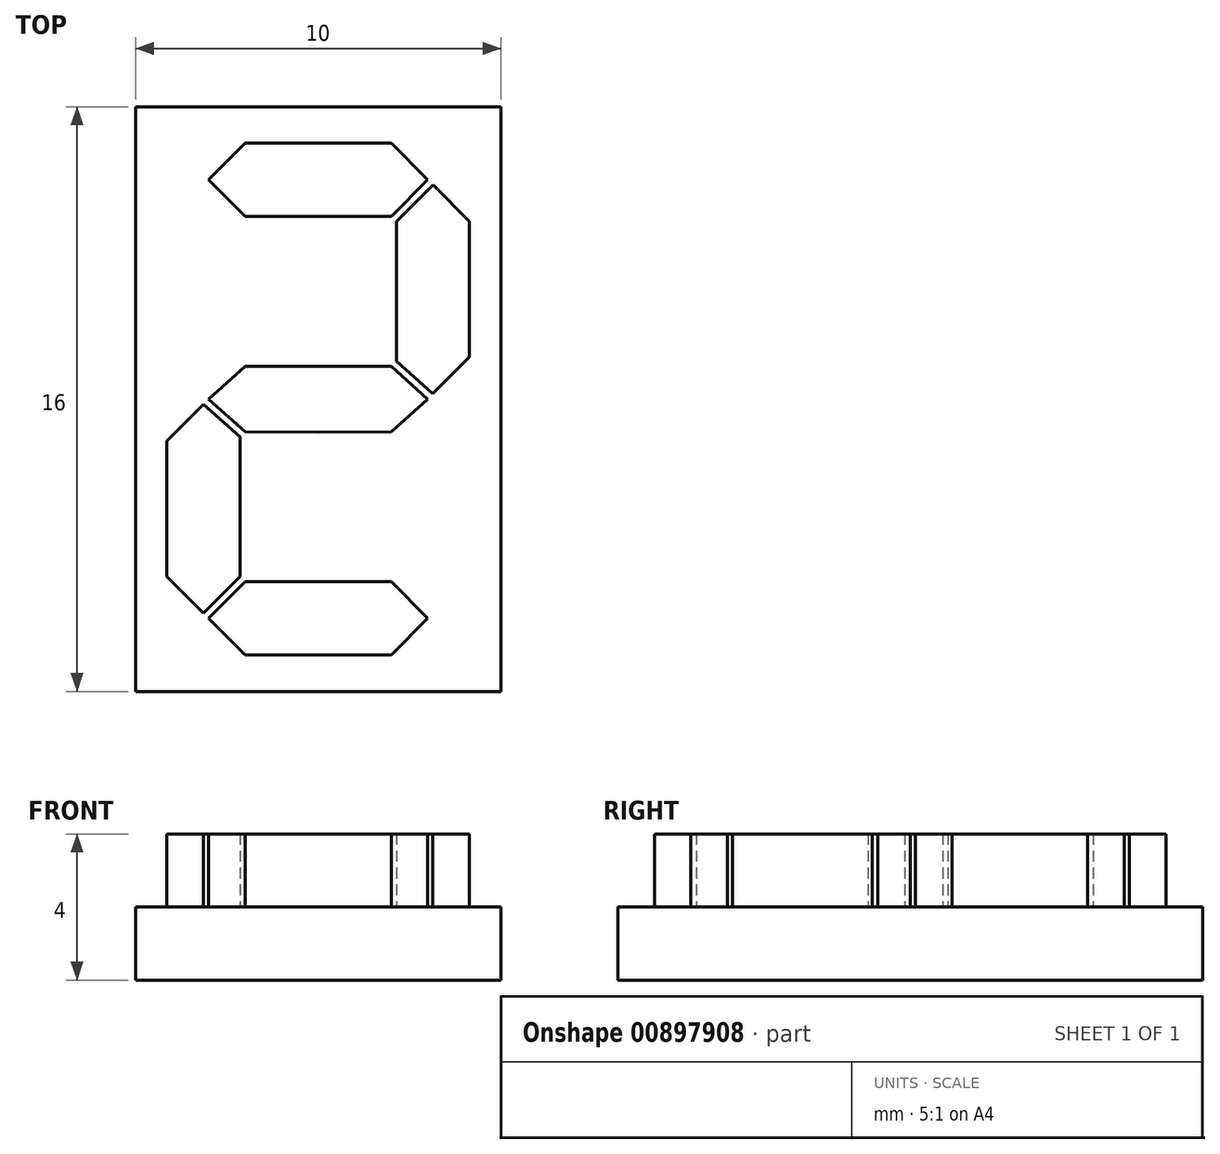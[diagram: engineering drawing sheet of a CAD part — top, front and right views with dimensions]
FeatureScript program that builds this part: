
annotation { "Feature Type Name" : "Feature", "Feature Type Description" : "" }
export const myFeature = defineFeature(function(context is Context, id is Id, definition is map)
    precondition{}
    {
        {
            var Q0;
            Q0=qCreatedBy(makeId("Top.planeOp"),FACE);
            var sketch = newSketch(context, id + "F0", { "sketchPlane" : qUnion([Q0])});
            skLineSegment(sketch, "E0.bottom", {"start": v(5, -8) * mm, "end": v(-5, -8) * mm});
            skLineSegment(sketch, "E0.top", {"start": v(5, 8) * mm, "end": v(-5, 8) * mm});
            skLineSegment(sketch, "E0.left", {"start": v(5, -8) * mm, "end": v(5, 8) * mm});
            skLineSegment(sketch, "E0.right", {"start": v(-5, -8) * mm, "end": v(-5, 8) * mm});
            skPoint(sketch, "E0.middle", {"position": v(0, 0) * mm});
            skSolve(sketch);
        }
        {
            var Q0;
            Q0=makeQuery(id+"F0.imprint","IMPRINT",FACE,{"disambiguationData":[TD([[makeQuery(id+"F0.imprint","IMPRINT",EDGE,{"derivedFrom":sQuery(id+"F0.wireOp",EDGE,"E0.bottom")}),-1.0]])]});
            extrude(context, id + "F1", {"entities" : qUnion([Q0]), "depth" : 2 * mm, "offsetDistance" : 25 * mm});
        }
        {
            var Q0;
            Q0=makeQuery(id+"F1.opExtrude","CAP_FACE",FACE,{"disambiguationData":[OSD([sQuery(id+"F0.wireOp",EDGE,"E0.bottom"),sQuery(id+"F0.wireOp",EDGE,"E0.top"),sQuery(id+"F0.wireOp",EDGE,"E0.left"),sQuery(id+"F0.wireOp",EDGE,"E0.right")])],"isStart":false});
            var sketch = newSketch(context, id + "F2", { "sketchPlane" : qUnion([Q0])});
            skLineSegment(sketch, "E1", {"start": v(-3, 8) * mm, "end": v(-3, -8) * mm, "construction": true});
            skLineSegment(sketch, "E2.0.1.0", {"start": v(-5, 6) * mm, "end": v(5, 6) * mm, "construction": true});
            skLineSegment(sketch, "E2.direction2", {"start": v(-5, 7) * mm, "end": v(-5, 6) * mm, "construction": true});
            skLineSegment(sketch, "E3.1.0.0", {"start": v(-2, 8) * mm, "end": v(-2, -8) * mm, "construction": true});
            skLineSegment(sketch, "E3.3.0.0", {"start": v(0, 8) * mm, "end": v(0, -8) * mm, "construction": true});
            skLineSegment(sketch, "E3.direction1", {"start": v(-3, -8) * mm, "end": v(-2, -8) * mm, "construction": true});
            skLineSegment(sketch, "E4", {"start": v(-2, 7) * mm, "end": v(-3, 6) * mm});
            skLineSegment(sketch, "E5", {"start": v(-3, 6) * mm, "end": v(-2, 5) * mm});
            skLineSegment(sketch, "E6", {"start": v(-2, 5) * mm, "end": v(0, 5) * mm});
            skLineSegment(sketch, "E7", {"start": v(-2, 7) * mm, "end": v(0, 7) * mm});
            skLineSegment(sketch, "E8", {"start": v(-4.14, 4.86) * mm, "end": v(5, 4.86) * mm, "construction": true});
            skLineSegment(sketch, "E9", {"start": v(0, 0.9) * mm, "end": v(-2, 0.9) * mm});
            skLineSegment(sketch, "E10", {"start": v(-2, 0.9) * mm, "end": v(-3, 0) * mm});
            skLineSegment(sketch, "E11", {"start": v(-3.14, 5.86) * mm, "end": v(-3.14, 0.15) * mm, "construction": true});
            skLineSegment(sketch, "E12.MirrorCS", {"start": v(0, -0.9) * mm, "end": v(-2, -0.9) * mm});
            skLineSegment(sketch, "E13.MirrorCS", {"start": v(-2, -0.9) * mm, "end": v(-3, 0) * mm});
            skLineSegment(sketch, "E14.MirrorCS", {"start": v(-2, -5) * mm, "end": v(0, -5) * mm});
            skLineSegment(sketch, "E15.MirrorCS", {"start": v(-3, -6) * mm, "end": v(-2, -5) * mm});
            skLineSegment(sketch, "E16.MirrorCS", {"start": v(-2, -7) * mm, "end": v(-3, -6) * mm});
            skLineSegment(sketch, "E17.MirrorCS", {"start": v(-2, -7) * mm, "end": v(0, -7) * mm});
            skLineSegment(sketch, "E18.MirrorCS", {"start": v(-3.14, -5.86) * mm, "end": v(-2.14, -4.86) * mm});
            skLineSegment(sketch, "E19.MirrorCS", {"start": v(-3.14, -5.86) * mm, "end": v(-4.14, -4.86) * mm});
            skLineSegment(sketch, "E20.MirrorCS", {"start": v(-4.14, -4.86) * mm, "end": v(-4.14, -1.15) * mm});
            skLineSegment(sketch, "E21.MirrorCS", {"start": v(-4.14, -1.15) * mm, "end": v(-3.14, -0.15) * mm});
            skLineSegment(sketch, "E22.MirrorCS", {"start": v(-2.14, -4.86) * mm, "end": v(-2.14, -1.03) * mm});
            skLineSegment(sketch, "E23.MirrorCS", {"start": v(-2.14, -1.03) * mm, "end": v(-3.14, -0.15) * mm});
            skLineSegment(sketch, "E24.MirrorCS", {"start": v(2, 7) * mm, "end": v(0, 7) * mm});
            skLineSegment(sketch, "E25.MirrorCS", {"start": v(2, 7) * mm, "end": v(3, 6) * mm});
            skLineSegment(sketch, "E26.MirrorCS", {"start": v(3, 6) * mm, "end": v(2, 5) * mm});
            skLineSegment(sketch, "E27.MirrorCS", {"start": v(2, 5) * mm, "end": v(0, 5) * mm});
            skLineSegment(sketch, "E28.MirrorCS", {"start": v(3.14, 5.86) * mm, "end": v(2.14, 4.86) * mm});
            skLineSegment(sketch, "E29.MirrorCS", {"start": v(3.14, 5.86) * mm, "end": v(4.14, 4.86) * mm});
            skLineSegment(sketch, "E30.MirrorCS", {"start": v(4.14, 4.86) * mm, "end": v(4.14, 1.15) * mm});
            skLineSegment(sketch, "E31.MirrorCS", {"start": v(4.14, 1.15) * mm, "end": v(3.14, 0.15) * mm});
            skLineSegment(sketch, "E32.MirrorCS", {"start": v(2.14, 4.86) * mm, "end": v(2.14, 1.03) * mm});
            skLineSegment(sketch, "E33.MirrorCS", {"start": v(2.14, 1.03) * mm, "end": v(3.14, 0.15) * mm});
            skLineSegment(sketch, "E34.MirrorCS", {"start": v(2, 0.9) * mm, "end": v(3, 0) * mm});
            skLineSegment(sketch, "E35.MirrorCS", {"start": v(0, 0.9) * mm, "end": v(2, 0.9) * mm});
            skLineSegment(sketch, "E36.MirrorCS", {"start": v(2, -0.9) * mm, "end": v(3, 0) * mm});
            skLineSegment(sketch, "E37.MirrorCS", {"start": v(0, -0.9) * mm, "end": v(2, -0.9) * mm});
            skLineSegment(sketch, "E38.MirrorCS", {"start": v(3, -6) * mm, "end": v(2, -5) * mm});
            skLineSegment(sketch, "E39.MirrorCS", {"start": v(2, -5) * mm, "end": v(0, -5) * mm});
            skLineSegment(sketch, "E40.MirrorCS", {"start": v(2, -7) * mm, "end": v(3, -6) * mm});
            skLineSegment(sketch, "E41.MirrorCS", {"start": v(2, -7) * mm, "end": v(0, -7) * mm});
            skSolve(sketch);
        }
        {
            var Q0;
            Q0=qSketchRegion(id+"F2",true);
            extrude(context, id + "F3", {"entities" : qUnion([Q0]), "operationType" : NewBodyOperationType.ADD, "depth" : 2 * mm, "offsetDistance" : 25 * mm});
        }
    });
